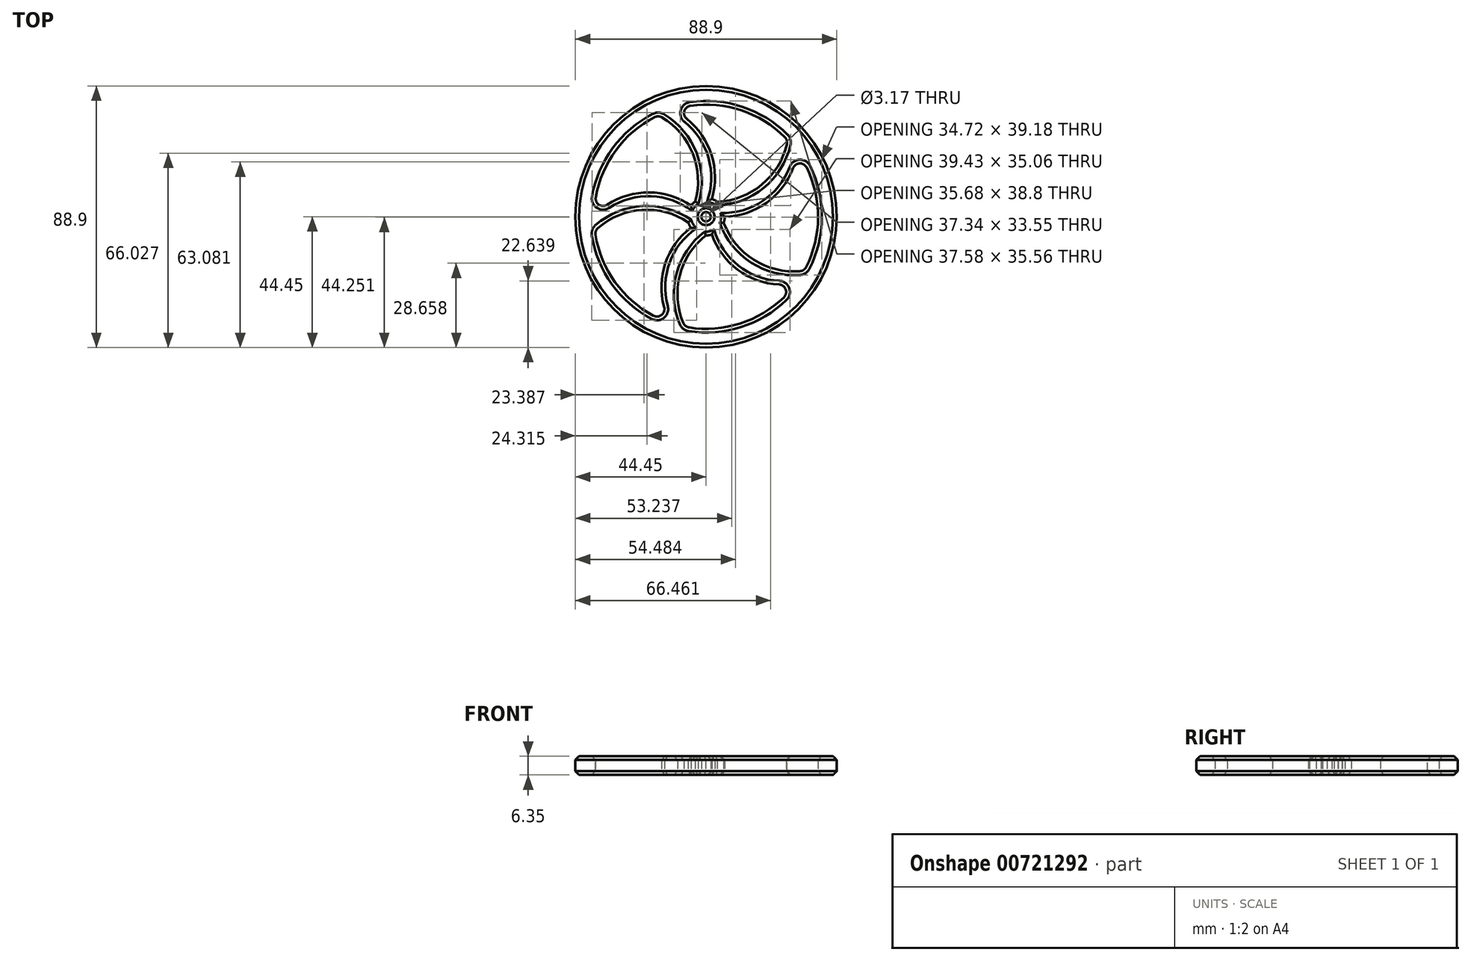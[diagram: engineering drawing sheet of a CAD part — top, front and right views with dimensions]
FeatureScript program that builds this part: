
annotation { "Feature Type Name" : "Feature", "Feature Type Description" : "" }
export const myFeature = defineFeature(function(context is Context, id is Id, definition is map)
    precondition{}
    {
        {
            var Q0;
            Q0=qCreatedBy(makeId("Top.planeOp"),FACE);
            var sketch = newSketch(context, id + "F0", { "sketchPlane" : qUnion([Q0])});
            skCircle(sketch, "E0", {"center": v(0, 0) * mm, "radius": 38.1 * mm});
            skCircle(sketch, "E1", {"center": v(0, 0) * mm, "radius": 6.35 * mm});
            skArc(sketch, "E2", {"start": v(6.35, 0) * mm, "mid": v(22.78, 6.5) * mm, "end": v(31, 22.16) * mm});
            skArc(sketch, "E3", {"start": v(3.81, 5.08) * mm, "mid": v(19.5, 11.36) * mm, "end": v(27.77, 26.08) * mm});
            skCircle(sketch, "E4.0", {"center": v(0, 0) * mm, "radius": 44.45 * mm});
            skArc(sketch, "E5.1.0", {"start": v(1.96, 6.04) * mm, "mid": v(0.85, 23.68) * mm, "end": v(-11.5, 36.32) * mm});
            skArc(sketch, "E5.1.1", {"start": v(-3.65, 5.2) * mm, "mid": v(-4.78, 22.05) * mm, "end": v(-16.23, 34.47) * mm});
            skArc(sketch, "E5.2.0", {"start": v(-5.14, 3.73) * mm, "mid": v(-22.26, 8.13) * mm, "end": v(-38.1, 0.3) * mm});
            skArc(sketch, "E5.2.1", {"start": v(-6.07, -1.87) * mm, "mid": v(-22.45, 2.27) * mm, "end": v(-37.8, -4.78) * mm});
            skArc(sketch, "E5.3.0", {"start": v(-5.14, -3.73) * mm, "mid": v(-14.6, -18.66) * mm, "end": v(-12.05, -36.14) * mm});
            skArc(sketch, "E5.3.1", {"start": v(-0.1, -6.35) * mm, "mid": v(-9.1, -20.65) * mm, "end": v(-7.13, -37.43) * mm});
            skArc(sketch, "E5.4.0", {"start": v(1.96, -6.04) * mm, "mid": v(13.23, -19.66) * mm, "end": v(30.65, -22.63) * mm});
            skArc(sketch, "E5.4.1", {"start": v(6, -2.05) * mm, "mid": v(16.83, -15.03) * mm, "end": v(33.39, -18.35) * mm});
            skCircle(sketch, "E6", {"center": v(0, 0) * mm, "radius": 1.59 * mm});
            skSolve(sketch);
        }
        {
            var Q0;
            {var subQ0=sQuery(id+"F0.wireOp",EDGE,"E5.4.0");Q0=makeQuery(id+"F0.imprint","IMPRINT",FACE,{"disambiguationData":[TD([[makeQuery(id+"F0.imprint","IMPRINT",EDGE,{"derivedFrom":subQ0}),1.0]])]});}
            var Q1;
            Q1=makeQuery(id+"F0.imprint","IMPRINT",FACE,{"disambiguationData":[TD([[makeQuery(id+"F0.imprint","IMPRINT",EDGE,{"derivedFrom":sQuery(id+"F0.wireOp",EDGE,"E6")}),-1.0]])]});
            var Q2;
            {var subQ0=sQuery(id+"F0.wireOp",EDGE,"E5.3.0");Q2=makeQuery(id+"F0.imprint","IMPRINT",FACE,{"disambiguationData":[TD([[makeQuery(id+"F0.imprint","IMPRINT",EDGE,{"derivedFrom":subQ0}),1.0]])]});}
            var Q3;
            {var subQ0=sQuery(id+"F0.wireOp",EDGE,"E5.2.0");Q3=makeQuery(id+"F0.imprint","IMPRINT",FACE,{"disambiguationData":[TD([[makeQuery(id+"F0.imprint","IMPRINT",EDGE,{"derivedFrom":subQ0}),1.0]])]});}
            var Q4;
            {var subQ0=sQuery(id+"F0.wireOp",EDGE,"E5.1.0");Q4=makeQuery(id+"F0.imprint","IMPRINT",FACE,{"disambiguationData":[TD([[makeQuery(id+"F0.imprint","IMPRINT",EDGE,{"derivedFrom":subQ0}),1.0]])]});}
            var Q5;
            {var subQ0=sQuery(id+"F0.wireOp",EDGE,"E2");Q5=makeQuery(id+"F0.imprint","IMPRINT",FACE,{"disambiguationData":[TD([[makeQuery(id+"F0.imprint","IMPRINT",EDGE,{"derivedFrom":subQ0}),1.0]])]});}
            var Q6;
            Q6=makeQuery(id+"F0.imprint","IMPRINT",FACE,{"disambiguationData":[TD([[makeQuery(id+"F0.imprint","IMPRINT",EDGE,{"derivedFrom":sQuery(id+"F0.wireOp",EDGE,"E4.0")}),1.0]])]});
            extrude(context, id + "F1", {"entities" : qUnion([Q0, Q1, Q2, Q3, Q4, Q5, Q6]), "depth" : 6.35 * mm, "offsetDistance" : 25.4 * mm});
        }
        {
            var Q0;
            Q0=makeQuery(id+"F1.opExtrude","SWEPT_EDGE",EDGE,{"disambiguationData":[OSD([sQuery(id+"F0.wireOp",EDGE,"E0"),sQuery(id+"F0.wireOp",EDGE,"E5.2.1")])]});
            var Q1;
            Q1=makeQuery(id+"F1.opExtrude","SWEPT_EDGE",EDGE,{"disambiguationData":[OSD([sQuery(id+"F0.wireOp",EDGE,"E0"),sQuery(id+"F0.wireOp",EDGE,"E5.2.0")])]});
            var Q2;
            Q2=makeQuery(id+"F1.opExtrude","SWEPT_EDGE",EDGE,{"disambiguationData":[OSD([sQuery(id+"F0.wireOp",EDGE,"E0"),sQuery(id+"F0.wireOp",EDGE,"E5.1.1")])]});
            var Q3;
            Q3=makeQuery(id+"F1.opExtrude","SWEPT_EDGE",EDGE,{"disambiguationData":[OSD([sQuery(id+"F0.wireOp",EDGE,"E0"),sQuery(id+"F0.wireOp",EDGE,"E5.1.0")])]});
            var Q4;
            Q4=makeQuery(id+"F1.opExtrude","SWEPT_EDGE",EDGE,{"disambiguationData":[OSD([sQuery(id+"F0.wireOp",EDGE,"E0"),sQuery(id+"F0.wireOp",EDGE,"E2")])]});
            var Q5;
            Q5=makeQuery(id+"F1.opExtrude","SWEPT_EDGE",EDGE,{"disambiguationData":[OSD([sQuery(id+"F0.wireOp",EDGE,"E0"),sQuery(id+"F0.wireOp",EDGE,"E3")])]});
            var Q6;
            Q6=makeQuery(id+"F1.opExtrude","SWEPT_EDGE",EDGE,{"disambiguationData":[OSD([sQuery(id+"F0.wireOp",EDGE,"E0"),sQuery(id+"F0.wireOp",EDGE,"E5.4.0")])]});
            var Q7;
            Q7=makeQuery(id+"F1.opExtrude","SWEPT_EDGE",EDGE,{"disambiguationData":[OSD([sQuery(id+"F0.wireOp",EDGE,"E0"),sQuery(id+"F0.wireOp",EDGE,"E5.4.1")])]});
            var Q8;
            Q8=makeQuery(id+"F1.opExtrude","SWEPT_EDGE",EDGE,{"disambiguationData":[OSD([sQuery(id+"F0.wireOp",EDGE,"E0"),sQuery(id+"F0.wireOp",EDGE,"E5.3.0")])]});
            var Q9;
            Q9=makeQuery(id+"F1.opExtrude","SWEPT_EDGE",EDGE,{"disambiguationData":[OSD([sQuery(id+"F0.wireOp",EDGE,"E0"),sQuery(id+"F0.wireOp",EDGE,"E5.3.1")])]});
            fillet(context, id + "F2", {"entities" : qUnion([Q0, Q1, Q2, Q3, Q4, Q5, Q6, Q7, Q8, Q9]), "radius" : 2.54 * mm, "tangentPropagation" : true, "allowEdgeOverflow" : false});
        }
        {
            var Q0;
            Q0=makeQuery(id+"F1.opExtrude","CAP_FACE",FACE,{"disambiguationData":[OSD([sQuery(id+"F0.wireOp",EDGE,"E0"),sQuery(id+"F0.wireOp",EDGE,"E1"),sQuery(id+"F0.wireOp",EDGE,"E2"),sQuery(id+"F0.wireOp",EDGE,"E3"),sQuery(id+"F0.wireOp",EDGE,"E4.0"),sQuery(id+"F0.wireOp",EDGE,"E5.1.0"),sQuery(id+"F0.wireOp",EDGE,"E5.1.1"),sQuery(id+"F0.wireOp",EDGE,"E5.2.0"),sQuery(id+"F0.wireOp",EDGE,"E5.2.1"),sQuery(id+"F0.wireOp",EDGE,"E5.3.0"),sQuery(id+"F0.wireOp",EDGE,"E5.3.1"),sQuery(id+"F0.wireOp",EDGE,"E5.4.0"),sQuery(id+"F0.wireOp",EDGE,"E5.4.1"),sQuery(id+"F0.wireOp",EDGE,"E6")])],"isStart":false});
            var Q1;
            Q1=makeQuery(id+"F1.opExtrude","CAP_FACE",FACE,{"disambiguationData":[OSD([sQuery(id+"F0.wireOp",EDGE,"E0"),sQuery(id+"F0.wireOp",EDGE,"E1"),sQuery(id+"F0.wireOp",EDGE,"E2"),sQuery(id+"F0.wireOp",EDGE,"E3"),sQuery(id+"F0.wireOp",EDGE,"E4.0"),sQuery(id+"F0.wireOp",EDGE,"E5.1.0"),sQuery(id+"F0.wireOp",EDGE,"E5.1.1"),sQuery(id+"F0.wireOp",EDGE,"E5.2.0"),sQuery(id+"F0.wireOp",EDGE,"E5.2.1"),sQuery(id+"F0.wireOp",EDGE,"E5.3.0"),sQuery(id+"F0.wireOp",EDGE,"E5.3.1"),sQuery(id+"F0.wireOp",EDGE,"E5.4.0"),sQuery(id+"F0.wireOp",EDGE,"E5.4.1"),sQuery(id+"F0.wireOp",EDGE,"E6")])],"isStart":true});
            chamfer(context, id + "F3", {"entities" : qUnion([Q0, Q1]), "width" : 1.27 * mm, "tangentPropagation" : true});
        }
    });
